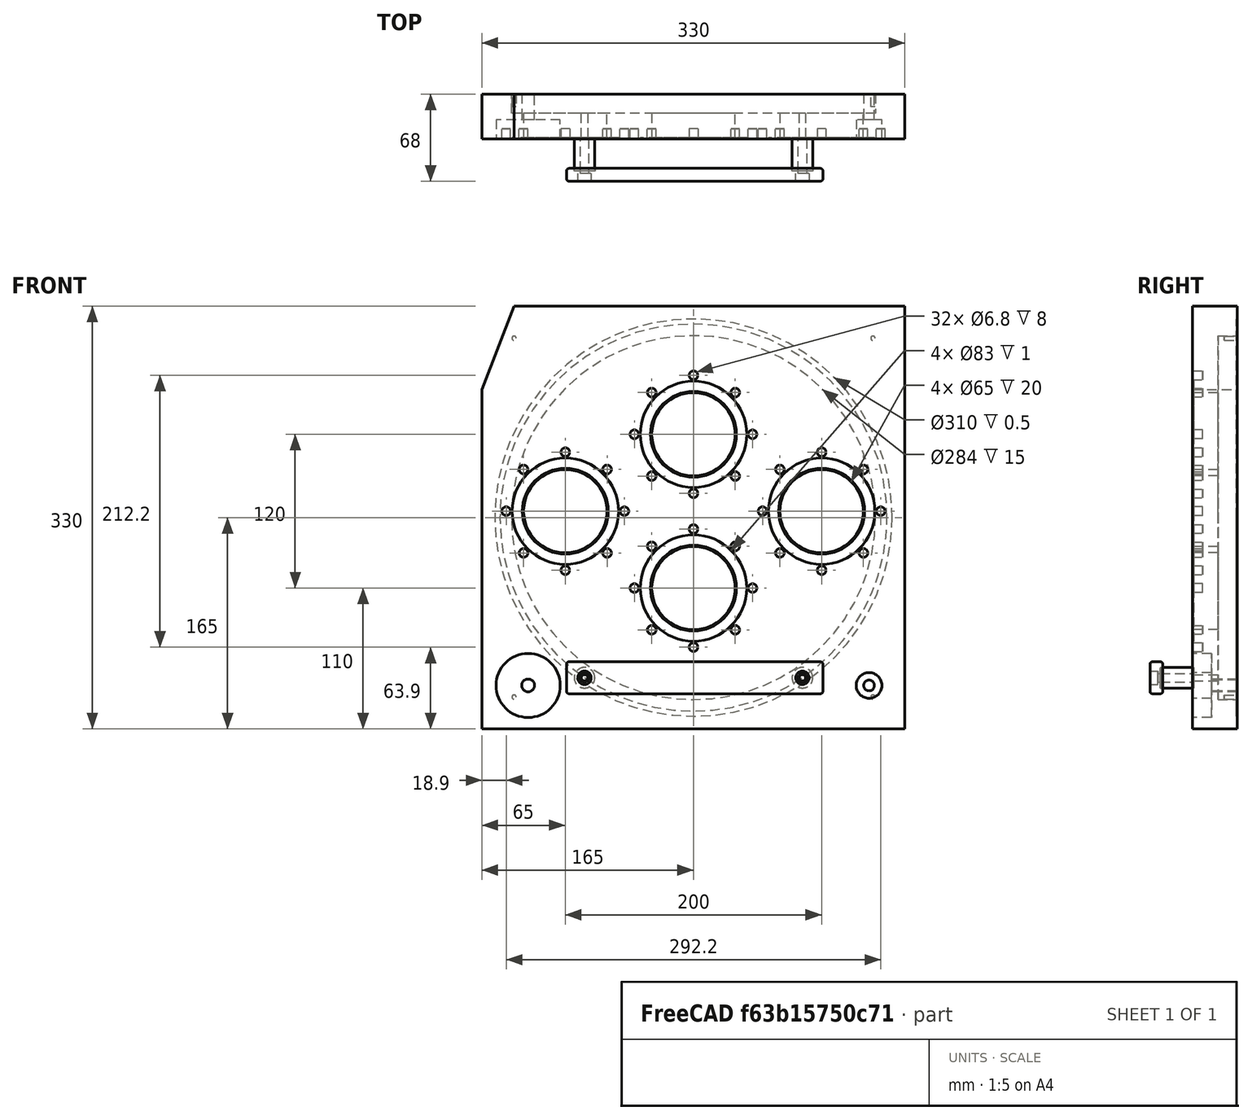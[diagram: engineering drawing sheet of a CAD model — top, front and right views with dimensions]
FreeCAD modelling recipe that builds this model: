
FCSTD DOCUMENT  (FreeCAD 0.21R33675 (Git))
Label: XL30Frontdoor_Flanges01
License: All rights reserved
LicenseURL: http://en.wikipedia.org/wiki/All_rights_reserved
objects: TechDraw::DrawViewDimension×68, Part::Cylinder×54, Part::Compound×28, TechDraw::DrawProjGroupItem×13, Part::Cut×11, Part::MultiFuse×10, TechDraw::DrawSVGTemplate×7, TechDraw::DrawProjGroup×7, TechDraw::DrawPage×7, TechDraw::DrawViewSection×6, Part::Feature×3, TechDraw::DrawViewAnnotation×3, App::Link×1, Part::Box×1, Part::Fillet×1, TechDraw::DrawViewPart×1
note: 214 computed .brp shape members not serialized (recipe doc carries the construction recipe); baked Part::Feature solids carry a one-line shape summary decoded from their .brp
EXTERNAL_REF file=XL30SimpleFrontdoor01.FCStd obj=Cut012_solid

FEATURE [App::Link] Link  label="XL30SimpleFrontdoor01"
  LinkedObject = -> <external XL30SimpleFrontdoor01.FCStd>#Cut012_solid
FEATURE [Part::Cylinder] Cylinder  label="Zylinder"
  Angle = 360
  AttacherType = Attacher::AttachEngine3D
  FirstAngle = 0
  Height = 40
  Placement = pos=(165,0,110) rot=(-1,0,0;1.5708rad)
  Radius = 32.5
  SecondAngle = 0
FEATURE [Part::Cylinder] Cylinder001  label="Zylinder001"
  Angle = 360
  AttacherType = Attacher::AttachEngine3D
  FirstAngle = 0
  Height = 1
  Placement = pos=(165,0,110) rot=(-1,0,0;1.5708rad)
  Radius = 41.5
  SecondAngle = 0
FEATURE [Part::Cylinder] Cylinder002  label="Zylinder002"
  Angle = 360
  AttacherType = Attacher::AttachEngine3D
  FirstAngle = 0
  Height = 1
  Placement = pos=(165,0,110) rot=(-1,0,0;1.5708rad)
  Radius = 33.5
  SecondAngle = 0
FEATURE [Part::Cut] Cut
  Base = -> Cylinder001
  Tool = -> Cylinder002
FEATURE [Part::Cylinder] Cylinder003  label="Zylinder003"
  Angle = 360
  AttacherType = Attacher::AttachEngine3D
  FirstAngle = 0
  Height = 8
  Placement = pos=(0,0,-46.1) rot=(1,0,0;1.5708rad)
  Radius = 3.4
  SecondAngle = 0
FEATURE [Part::Cylinder] Cylinder004  label="Zylinder004"
  Angle = 360
  AttacherType = Attacher::AttachEngine3D
  FirstAngle = 0
  Height = 8
  Placement = pos=(0,0,-46.1) rot=(1,0,0;1.5708rad)
  Radius = 3.4
  SecondAngle = 0
FEATURE [Part::Compound] Compound
  Links = -> [Cylinder004]
  Placement = pos=(0,0,0) rot=(0,1,0;0.785398rad)
FEATURE [Part::Cylinder] Cylinder005  label="Zylinder005"
  Angle = 360
  AttacherType = Attacher::AttachEngine3D
  FirstAngle = 0
  Height = 8
  Placement = pos=(0,0,-46.1) rot=(1,0,0;1.5708rad)
  Radius = 3.4
  SecondAngle = 0
FEATURE [Part::Compound] Compound001
  Links = -> [Cylinder005]
  Placement = pos=(0,0,0) rot=(0,1,0;1.5708rad)
FEATURE [Part::Cylinder] Cylinder006  label="Zylinder006"
  Angle = 360
  AttacherType = Attacher::AttachEngine3D
  FirstAngle = 0
  Height = 8
  Placement = pos=(0,0,-46.1) rot=(1,0,0;1.5708rad)
  Radius = 3.4
  SecondAngle = 0
FEATURE [Part::Compound] Compound002
  Links = -> [Cylinder006]
  Placement = pos=(0,0,0) rot=(0,1,0;2.35619rad)
FEATURE [Part::Cylinder] Cylinder007  label="Zylinder007"
  Angle = 360
  AttacherType = Attacher::AttachEngine3D
  FirstAngle = 0
  Height = 8
  Placement = pos=(0,0,-46.1) rot=(1,0,0;1.5708rad)
  Radius = 3.4
  SecondAngle = 0
FEATURE [Part::Compound] Compound003
  Links = -> [Cylinder007]
  Placement = pos=(0,0,0) rot=(0,1,0;3.14159rad)
FEATURE [Part::Cylinder] Cylinder008  label="Zylinder008"
  Angle = 360
  AttacherType = Attacher::AttachEngine3D
  FirstAngle = 0
  Height = 8
  Placement = pos=(0,0,-46.1) rot=(1,0,0;1.5708rad)
  Radius = 3.4
  SecondAngle = 0
FEATURE [Part::Compound] Compound004
  Links = -> [Cylinder008]
  Placement = pos=(0,0,0) rot=(0,1,0;3.92699rad)
FEATURE [Part::Cylinder] Cylinder009  label="Zylinder009"
  Angle = 360
  AttacherType = Attacher::AttachEngine3D
  FirstAngle = 0
  Height = 8
  Placement = pos=(0,0,-46.1) rot=(1,0,0;1.5708rad)
  Radius = 3.4
  SecondAngle = 0
FEATURE [Part::Compound] Compound005
  Links = -> [Cylinder009]
  Placement = pos=(0,0,0) rot=(0,-1,0;1.5708rad)
FEATURE [Part::Cylinder] Cylinder010  label="Zylinder010"
  Angle = 360
  AttacherType = Attacher::AttachEngine3D
  FirstAngle = 0
  Height = 8
  Placement = pos=(0,0,-46.1) rot=(1,0,0;1.5708rad)
  Radius = 3.4
  SecondAngle = 0
FEATURE [Part::Compound] Compound006
  Links = -> [Cylinder010]
  Placement = pos=(0,0,0) rot=(0,-1,0;0.785398rad)
FEATURE [Part::MultiFuse] Fusion
  Placement = pos=(165,8,110) rot=(0,0,1;0rad)
  Shapes = -> [Compound006,Compound,Compound001,Compound002,Compound003,Compound004,Compound005,Cylinder003]
FEATURE [Part::MultiFuse] Fusion001
  Shapes = -> [Cut,Cylinder,Fusion]
FEATURE [Part::Cut] Cut001
  Base = -> Link
  Tool = -> Fusion001
FEATURE [Part::Cylinder] Cylinder011  label="Zylinder011"
  Angle = 360
  AttacherType = Attacher::AttachEngine3D
  FirstAngle = 0
  Height = 40
  Placement = pos=(165,0,110) rot=(-1,0,0;1.5708rad)
  Radius = 32.5
  SecondAngle = 0
FEATURE [Part::Cylinder] Cylinder012  label="Zylinder012"
  Angle = 360
  AttacherType = Attacher::AttachEngine3D
  FirstAngle = 0
  Height = 1
  Placement = pos=(165,0,110) rot=(-1,0,0;1.5708rad)
  Radius = 41.5
  SecondAngle = 0
FEATURE [Part::Cylinder] Cylinder013  label="Zylinder013"
  Angle = 360
  AttacherType = Attacher::AttachEngine3D
  FirstAngle = 0
  Height = 1
  Placement = pos=(165,0,110) rot=(-1,0,0;1.5708rad)
  Radius = 33.5
  SecondAngle = 0
FEATURE [Part::Cut] Cut002
  Base = -> Cylinder012
  Tool = -> Cylinder013
FEATURE [Part::Cylinder] Cylinder014  label="Zylinder014"
  Angle = 360
  AttacherType = Attacher::AttachEngine3D
  FirstAngle = 0
  Height = 8
  Placement = pos=(0,0,-46.1) rot=(1,0,0;1.5708rad)
  Radius = 3.4
  SecondAngle = 0
FEATURE [Part::Cylinder] Cylinder015  label="Zylinder015"
  Angle = 360
  AttacherType = Attacher::AttachEngine3D
  FirstAngle = 0
  Height = 8
  Placement = pos=(0,0,-46.1) rot=(1,0,0;1.5708rad)
  Radius = 3.4
  SecondAngle = 0
FEATURE [Part::Compound] Compound007
  Links = -> [Cylinder015]
  Placement = pos=(0,0,0) rot=(0,1,0;0.785398rad)
FEATURE [Part::Cylinder] Cylinder016  label="Zylinder016"
  Angle = 360
  AttacherType = Attacher::AttachEngine3D
  FirstAngle = 0
  Height = 8
  Placement = pos=(0,0,-46.1) rot=(1,0,0;1.5708rad)
  Radius = 3.4
  SecondAngle = 0
FEATURE [Part::Compound] Compound008
  Links = -> [Cylinder016]
  Placement = pos=(0,0,0) rot=(0,1,0;1.5708rad)
FEATURE [Part::Cylinder] Cylinder017  label="Zylinder017"
  Angle = 360
  AttacherType = Attacher::AttachEngine3D
  FirstAngle = 0
  Height = 8
  Placement = pos=(0,0,-46.1) rot=(1,0,0;1.5708rad)
  Radius = 3.4
  SecondAngle = 0
FEATURE [Part::Compound] Compound009
  Links = -> [Cylinder017]
  Placement = pos=(0,0,0) rot=(0,1,0;2.35619rad)
FEATURE [Part::Cylinder] Cylinder018  label="Zylinder018"
  Angle = 360
  AttacherType = Attacher::AttachEngine3D
  FirstAngle = 0
  Height = 8
  Placement = pos=(0,0,-46.1) rot=(1,0,0;1.5708rad)
  Radius = 3.4
  SecondAngle = 0
FEATURE [Part::Compound] Compound010
  Links = -> [Cylinder018]
  Placement = pos=(0,0,0) rot=(0,1,0;3.14159rad)
FEATURE [Part::Cylinder] Cylinder019  label="Zylinder019"
  Angle = 360
  AttacherType = Attacher::AttachEngine3D
  FirstAngle = 0
  Height = 8
  Placement = pos=(0,0,-46.1) rot=(1,0,0;1.5708rad)
  Radius = 3.4
  SecondAngle = 0
FEATURE [Part::Compound] Compound011
  Links = -> [Cylinder019]
  Placement = pos=(0,0,0) rot=(0,1,0;3.92699rad)
FEATURE [Part::Cylinder] Cylinder020  label="Zylinder020"
  Angle = 360
  AttacherType = Attacher::AttachEngine3D
  FirstAngle = 0
  Height = 8
  Placement = pos=(0,0,-46.1) rot=(1,0,0;1.5708rad)
  Radius = 3.4
  SecondAngle = 0
FEATURE [Part::Compound] Compound012
  Links = -> [Cylinder020]
  Placement = pos=(0,0,0) rot=(0,-1,0;1.5708rad)
FEATURE [Part::Cylinder] Cylinder021  label="Zylinder021"
  Angle = 360
  AttacherType = Attacher::AttachEngine3D
  FirstAngle = 0
  Height = 8
  Placement = pos=(0,0,-46.1) rot=(1,0,0;1.5708rad)
  Radius = 3.4
  SecondAngle = 0
FEATURE [Part::Compound] Compound013
  Links = -> [Cylinder021]
  Placement = pos=(0,0,0) rot=(0,-1,0;0.785398rad)
FEATURE [Part::MultiFuse] Fusion002
  Placement = pos=(165,8,110) rot=(0,0,1;0rad)
  Shapes = -> [Compound013,Compound007,Compound008,Compound009,Compound010,Compound011,Compound012,Cylinder014]
FEATURE [Part::MultiFuse] Fusion003
  Placement = pos=(0,0,120) rot=(0,0,1;0rad)
  Shapes = -> [Cut002,Cylinder011,Fusion002]
FEATURE [Part::Cylinder] Cylinder022  label="Zylinder022"
  Angle = 360
  AttacherType = Attacher::AttachEngine3D
  FirstAngle = 0
  Height = 40
  Placement = pos=(165,0,110) rot=(-1,0,0;1.5708rad)
  Radius = 32.5
  SecondAngle = 0
FEATURE [Part::Cylinder] Cylinder023  label="Zylinder023"
  Angle = 360
  AttacherType = Attacher::AttachEngine3D
  FirstAngle = 0
  Height = 1
  Placement = pos=(165,0,110) rot=(-1,0,0;1.5708rad)
  Radius = 41.5
  SecondAngle = 0
FEATURE [Part::Cylinder] Cylinder024  label="Zylinder024"
  Angle = 360
  AttacherType = Attacher::AttachEngine3D
  FirstAngle = 0
  Height = 1
  Placement = pos=(165,0,110) rot=(-1,0,0;1.5708rad)
  Radius = 33.5
  SecondAngle = 0
FEATURE [Part::Cut] Cut003
  Base = -> Cylinder023
  Tool = -> Cylinder024
FEATURE [Part::Cylinder] Cylinder025  label="Zylinder025"
  Angle = 360
  AttacherType = Attacher::AttachEngine3D
  FirstAngle = 0
  Height = 8
  Placement = pos=(0,0,-46.1) rot=(1,0,0;1.5708rad)
  Radius = 3.4
  SecondAngle = 0
FEATURE [Part::Cylinder] Cylinder026  label="Zylinder026"
  Angle = 360
  AttacherType = Attacher::AttachEngine3D
  FirstAngle = 0
  Height = 8
  Placement = pos=(0,0,-46.1) rot=(1,0,0;1.5708rad)
  Radius = 3.4
  SecondAngle = 0
FEATURE [Part::Compound] Compound014
  Links = -> [Cylinder026]
  Placement = pos=(0,0,0) rot=(0,1,0;0.785398rad)
FEATURE [Part::Cylinder] Cylinder027  label="Zylinder027"
  Angle = 360
  AttacherType = Attacher::AttachEngine3D
  FirstAngle = 0
  Height = 8
  Placement = pos=(0,0,-46.1) rot=(1,0,0;1.5708rad)
  Radius = 3.4
  SecondAngle = 0
FEATURE [Part::Compound] Compound015
  Links = -> [Cylinder027]
  Placement = pos=(0,0,0) rot=(0,1,0;1.5708rad)
FEATURE [Part::Cylinder] Cylinder028  label="Zylinder028"
  Angle = 360
  AttacherType = Attacher::AttachEngine3D
  FirstAngle = 0
  Height = 8
  Placement = pos=(0,0,-46.1) rot=(1,0,0;1.5708rad)
  Radius = 3.4
  SecondAngle = 0
FEATURE [Part::Compound] Compound016
  Links = -> [Cylinder028]
  Placement = pos=(0,0,0) rot=(0,1,0;2.35619rad)
FEATURE [Part::Cylinder] Cylinder029  label="Zylinder029"
  Angle = 360
  AttacherType = Attacher::AttachEngine3D
  FirstAngle = 0
  Height = 8
  Placement = pos=(0,0,-46.1) rot=(1,0,0;1.5708rad)
  Radius = 3.4
  SecondAngle = 0
FEATURE [Part::Compound] Compound017
  Links = -> [Cylinder029]
  Placement = pos=(0,0,0) rot=(0,1,0;3.14159rad)
FEATURE [Part::Cylinder] Cylinder030  label="Zylinder030"
  Angle = 360
  AttacherType = Attacher::AttachEngine3D
  FirstAngle = 0
  Height = 8
  Placement = pos=(0,0,-46.1) rot=(1,0,0;1.5708rad)
  Radius = 3.4
  SecondAngle = 0
FEATURE [Part::Compound] Compound018
  Links = -> [Cylinder030]
  Placement = pos=(0,0,0) rot=(0,1,0;3.92699rad)
FEATURE [Part::Cylinder] Cylinder031  label="Zylinder031"
  Angle = 360
  AttacherType = Attacher::AttachEngine3D
  FirstAngle = 0
  Height = 8
  Placement = pos=(0,0,-46.1) rot=(1,0,0;1.5708rad)
  Radius = 3.4
  SecondAngle = 0
FEATURE [Part::Compound] Compound019
  Links = -> [Cylinder031]
  Placement = pos=(0,0,0) rot=(0,-1,0;1.5708rad)
FEATURE [Part::Cylinder] Cylinder032  label="Zylinder032"
  Angle = 360
  AttacherType = Attacher::AttachEngine3D
  FirstAngle = 0
  Height = 8
  Placement = pos=(0,0,-46.1) rot=(1,0,0;1.5708rad)
  Radius = 3.4
  SecondAngle = 0
FEATURE [Part::Compound] Compound020
  Links = -> [Cylinder032]
  Placement = pos=(0,0,0) rot=(0,-1,0;0.785398rad)
FEATURE [Part::MultiFuse] Fusion004
  Placement = pos=(165,8,110) rot=(0,0,1;0rad)
  Shapes = -> [Compound020,Compound014,Compound015,Compound016,Compound017,Compound018,Compound019,Cylinder025]
FEATURE [Part::MultiFuse] Fusion005
  Placement = pos=(-100,0,60) rot=(0,0,1;0rad)
  Shapes = -> [Cut003,Cylinder022,Fusion004]
FEATURE [Part::Cylinder] Cylinder033  label="Zylinder033"
  Angle = 360
  AttacherType = Attacher::AttachEngine3D
  FirstAngle = 0
  Height = 40
  Placement = pos=(165,0,110) rot=(-1,0,0;1.5708rad)
  Radius = 32.5
  SecondAngle = 0
FEATURE [Part::Cylinder] Cylinder034  label="Zylinder034"
  Angle = 360
  AttacherType = Attacher::AttachEngine3D
  FirstAngle = 0
  Height = 1
  Placement = pos=(165,0,110) rot=(-1,0,0;1.5708rad)
  Radius = 41.5
  SecondAngle = 0
FEATURE [Part::Cylinder] Cylinder035  label="Zylinder035"
  Angle = 360
  AttacherType = Attacher::AttachEngine3D
  FirstAngle = 0
  Height = 1
  Placement = pos=(165,0,110) rot=(-1,0,0;1.5708rad)
  Radius = 33.5
  SecondAngle = 0
FEATURE [Part::Cut] Cut004
  Base = -> Cylinder034
  Tool = -> Cylinder035
FEATURE [Part::Cylinder] Cylinder036  label="Zylinder036"
  Angle = 360
  AttacherType = Attacher::AttachEngine3D
  FirstAngle = 0
  Height = 8
  Placement = pos=(0,0,-46.1) rot=(1,0,0;1.5708rad)
  Radius = 3.4
  SecondAngle = 0
FEATURE [Part::Cylinder] Cylinder037  label="Zylinder037"
  Angle = 360
  AttacherType = Attacher::AttachEngine3D
  FirstAngle = 0
  Height = 8
  Placement = pos=(0,0,-46.1) rot=(1,0,0;1.5708rad)
  Radius = 3.4
  SecondAngle = 0
FEATURE [Part::Compound] Compound021
  Links = -> [Cylinder037]
  Placement = pos=(0,0,0) rot=(0,1,0;0.785398rad)
FEATURE [Part::Cylinder] Cylinder038  label="Zylinder038"
  Angle = 360
  AttacherType = Attacher::AttachEngine3D
  FirstAngle = 0
  Height = 8
  Placement = pos=(0,0,-46.1) rot=(1,0,0;1.5708rad)
  Radius = 3.4
  SecondAngle = 0
FEATURE [Part::Compound] Compound022
  Links = -> [Cylinder038]
  Placement = pos=(0,0,0) rot=(0,1,0;1.5708rad)
FEATURE [Part::Cylinder] Cylinder039  label="Zylinder039"
  Angle = 360
  AttacherType = Attacher::AttachEngine3D
  FirstAngle = 0
  Height = 8
  Placement = pos=(0,0,-46.1) rot=(1,0,0;1.5708rad)
  Radius = 3.4
  SecondAngle = 0
FEATURE [Part::Compound] Compound023
  Links = -> [Cylinder039]
  Placement = pos=(0,0,0) rot=(0,1,0;2.35619rad)
FEATURE [Part::Cylinder] Cylinder040  label="Zylinder040"
  Angle = 360
  AttacherType = Attacher::AttachEngine3D
  FirstAngle = 0
  Height = 8
  Placement = pos=(0,0,-46.1) rot=(1,0,0;1.5708rad)
  Radius = 3.4
  SecondAngle = 0
FEATURE [Part::Compound] Compound024
  Links = -> [Cylinder040]
  Placement = pos=(0,0,0) rot=(0,1,0;3.14159rad)
FEATURE [Part::Cylinder] Cylinder041  label="Zylinder041"
  Angle = 360
  AttacherType = Attacher::AttachEngine3D
  FirstAngle = 0
  Height = 8
  Placement = pos=(0,0,-46.1) rot=(1,0,0;1.5708rad)
  Radius = 3.4
  SecondAngle = 0
FEATURE [Part::Compound] Compound025
  Links = -> [Cylinder041]
  Placement = pos=(0,0,0) rot=(0,1,0;3.92699rad)
FEATURE [Part::Cylinder] Cylinder042  label="Zylinder042"
  Angle = 360
  AttacherType = Attacher::AttachEngine3D
  FirstAngle = 0
  Height = 8
  Placement = pos=(0,0,-46.1) rot=(1,0,0;1.5708rad)
  Radius = 3.4
  SecondAngle = 0
FEATURE [Part::Compound] Compound026
  Links = -> [Cylinder042]
  Placement = pos=(0,0,0) rot=(0,-1,0;1.5708rad)
FEATURE [Part::Cylinder] Cylinder043  label="Zylinder043"
  Angle = 360
  AttacherType = Attacher::AttachEngine3D
  FirstAngle = 0
  Height = 8
  Placement = pos=(0,0,-46.1) rot=(1,0,0;1.5708rad)
  Radius = 3.4
  SecondAngle = 0
FEATURE [Part::Compound] Compound027
  Links = -> [Cylinder043]
  Placement = pos=(0,0,0) rot=(0,-1,0;0.785398rad)
FEATURE [Part::MultiFuse] Fusion006
  Placement = pos=(165,8,110) rot=(0,0,1;0rad)
  Shapes = -> [Compound027,Compound021,Compound022,Compound023,Compound024,Compound025,Compound026,Cylinder036]
FEATURE [Part::MultiFuse] Fusion007
  Placement = pos=(100,0,60) rot=(0,0,1;0rad)
  Shapes = -> [Cut004,Cylinder033,Fusion006]
FEATURE [Part::MultiFuse] Fusion008
  Shapes = -> [Fusion003,Fusion007,Fusion005]
FEATURE [Part::Cut] Cut005  label="XL30FrontdoorCF64Flanges"
  Base = -> Cut001
  Tool = -> Fusion008
FEATURE [Part::Feature] Cut005_solid  label="XL30FrontdoorCF64Flanges (Solid)"
  shape: bbox 330 x 35 x 330 mm, 119 faces (baked)
FEATURE [Part::Box] Box002  label="Würfel002"
  AttacherType = Attacher::AttachEngine3D
  Height = 25
  Length = 200
  Placement = pos=(66,-28,27.5) rot=(0,0,1;0rad)
  Width = 10
FEATURE [Part::Cylinder] Cylinder044  label="Zylinder044"
  Angle = 360
  AttacherType = Attacher::AttachEngine3D
  FirstAngle = 0
  Height = 25
  Placement = pos=(80,0,40) rot=(1,0,0;1.5708rad)
  Radius = 8
  SecondAngle = 0
FEATURE [Part::Cylinder] Cylinder045  label="Zylinder045"
  Angle = 360
  AttacherType = Attacher::AttachEngine3D
  FirstAngle = 0
  Height = 25
  Placement = pos=(250,0,40) rot=(1,0,0;1.5708rad)
  Radius = 8
  SecondAngle = 0
FEATURE [Part::Cylinder] Cylinder046  label="Zylinder046"
  Angle = 360
  AttacherType = Attacher::AttachEngine3D
  FirstAngle = 0
  Height = 25
  Placement = pos=(80,0,40) rot=(1,0,0;1.5708rad)
  Radius = 3.3
  SecondAngle = 0
FEATURE [Part::Cut] Cut006  label="Spacer01"
  Base = -> Cylinder044
  Tool = -> Cylinder046
FEATURE [Part::Cylinder] Cylinder047  label="Zylinder047"
  Angle = 360
  AttacherType = Attacher::AttachEngine3D
  FirstAngle = 0
  Height = 25
  Placement = pos=(250,0,40) rot=(1,0,0;1.5708rad)
  Radius = 3.3
  SecondAngle = 0
FEATURE [Part::Cut] Cut007  label="Spacer02"
  Base = -> Cylinder045
  Tool = -> Cylinder047
FEATURE [Part::Cylinder] Cylinder048  label="Zylinder048"
  Angle = 360
  AttacherType = Attacher::AttachEngine3D
  FirstAngle = 0
  Height = 20
  Placement = pos=(80,0,40) rot=(1,0,0;1.5708rad)
  Radius = 8.1
  SecondAngle = 0
FEATURE [Part::Cut] Cut008
  Base = -> Box002
  Tool = -> Cylinder048
FEATURE [Part::Cylinder] Cylinder049  label="Zylinder049"
  Angle = 360
  AttacherType = Attacher::AttachEngine3D
  FirstAngle = 0
  Height = 20
  Placement = pos=(250,0,40) rot=(1,0,0;1.5708rad)
  Radius = 8.1
  SecondAngle = 0
FEATURE [Part::Cut] Cut009
  Base = -> Cut008
  Tool = -> Cylinder049
FEATURE [Part::Cylinder] Cylinder050  label="Zylinder050"
  Angle = 360
  AttacherType = Attacher::AttachEngine3D
  FirstAngle = 0
  Height = 6
  Placement = pos=(80,-22,40) rot=(1,0,0;1.5708rad)
  Radius = 5.2
  SecondAngle = 0
FEATURE [Part::Cylinder] Cylinder051  label="Zylinder051"
  Angle = 360
  AttacherType = Attacher::AttachEngine3D
  FirstAngle = 0
  Height = 6
  Placement = pos=(250,-22,40) rot=(1,0,0;1.5708rad)
  Radius = 5.2
  SecondAngle = 0
FEATURE [Part::Cylinder] Cylinder052  label="Zylinder052"
  Angle = 360
  AttacherType = Attacher::AttachEngine3D
  FirstAngle = 0
  Height = 20
  Placement = pos=(80,-10,40) rot=(1,0,0;1.5708rad)
  Radius = 3.3
  SecondAngle = 0
FEATURE [Part::Cylinder] Cylinder053  label="Zylinder053"
  Angle = 360
  AttacherType = Attacher::AttachEngine3D
  FirstAngle = 0
  Height = 20
  Placement = pos=(250,-10,40) rot=(1,0,0;1.5708rad)
  Radius = 3.3
  SecondAngle = 0
FEATURE [Part::MultiFuse] Fusion009
  Shapes = -> [Cylinder050,Cylinder051,Cylinder052,Cylinder053]
FEATURE [Part::Cut] Cut010  label="HandleWithoutPhases"
  Base = -> Cut009
  Tool = -> Fusion009
FEATURE [Part::Fillet] Fillet  label="HandleWithFillet"
  Base = -> Cut010
  Edges = 12 edges r=2: [Edge1,Edge2,Edge3,Edge4,Edge5,Edge6,Edge7,Edge10,Edge11,Edge12,Edge13,Edge16]
  Placement = pos=(0,-5,0) rot=(0,0,1;0rad)
FEATURE [Part::Feature] Cut006_solid  label="XL30FrontdoorCF64Flanges_Spacer"
  shape: bbox 16 x 25 x 16 mm, 4 faces (baked)
FEATURE [Part::Feature] Fillet_solid  label="XL30FrontdoorCF64Flanges_Handle"
  shape: bbox 200 x 10 x 25 mm, 36 faces (baked)
FEATURE [TechDraw::DrawSVGTemplate] Template
  EditableTexts = Designed_by_Name=Thomas Spielauer; Drawing_number=1; FC-Date=2023-09-05; FC-SC=mm; FC-SH=1/1; FC-Title=XL30 compatible flange door; Subtitle=Handle
  Height = 210
  Orientation = 1
  Template = <path>
  Width = 297
FEATURE [TechDraw::DrawProjGroupItem] ProjItem  label="Front"
  CoarseView = false
  Direction = (0,-1,0)
  Focus = 100
  HardHidden = false
  IsoCount = 0
  IsoHidden = false
  IsoVisible = false
  LockPosition = true
  Perspective = false
  Rotation = 0
  RotationVector = (1,0,0)
  ScaleType = 2
  ScrubCount = 0
  SeamHidden = false
  SeamVisible = false
  SmoothHidden = false
  SmoothVisible = true
  Source = -> [Fillet_solid]
  Type = 0
  X = 0
  XDirection = (1,0,0)
  Y = 0
FEATURE [TechDraw::DrawProjGroupItem] ProjItem001  label="Left"
  CoarseView = false
  Direction = (-1,-1e-16,0)
  Focus = 100
  HardHidden = false
  IsoCount = 0
  IsoHidden = false
  IsoVisible = false
  LockPosition = false
  Perspective = false
  Rotation = 0
  RotationVector = (1,0,0)
  ScaleType = 2
  ScrubCount = 0
  SeamHidden = false
  SeamVisible = false
  SmoothHidden = false
  SmoothVisible = true
  Source = -> [Fillet_solid]
  Type = 1
  X = 134.42
  XDirection = (1e-16,-1,0)
  Y = 0
FEATURE [TechDraw::DrawProjGroupItem] ProjItem002  label="Bottom"
  CoarseView = false
  Direction = (0,0,-1)
  Focus = 100
  HardHidden = false
  IsoCount = 0
  IsoHidden = false
  IsoVisible = false
  LockPosition = false
  Perspective = false
  Rotation = 0
  RotationVector = (1,0,0)
  ScaleType = 2
  ScrubCount = 0
  SeamHidden = false
  SeamVisible = false
  SmoothHidden = false
  SmoothVisible = true
  Source = -> [Fillet_solid]
  Type = 5
  X = 0
  XDirection = (1,0,0)
  Y = 41.7139
FEATURE [TechDraw::DrawProjGroup] ProjGroup
  Anchor = -> ProjItem
  AutoDistribute = false
  LockPosition = false
  ProjectionType = 0
  Rotation = 0
  ScaleType = 0
  Source = -> [Fillet_solid]
  Views = -> [ProjItem,ProjItem001,ProjItem002]
  X = 120.858
  Y = 131.49
  spacingX = 15
  spacingY = 15
FEATURE [TechDraw::DrawProjGroupItem] ProjItem003  label="Rückseite"
  CoarseView = false
  Direction = (0,1,0)
  Focus = 100
  HardHidden = false
  IsoCount = 0
  IsoHidden = false
  IsoVisible = false
  LockPosition = true
  Perspective = false
  Rotation = 0
  RotationVector = (-1,0,0)
  ScaleType = 2
  ScrubCount = 0
  SeamHidden = false
  SeamVisible = false
  SmoothHidden = false
  SmoothVisible = true
  Source = -> [Fillet_solid]
  Type = 0
  X = 0
  XDirection = (-1,0,0)
  Y = 0
FEATURE [TechDraw::DrawProjGroup] ProjGroup001
  Anchor = -> ProjItem003
  AutoDistribute = true
  LockPosition = false
  ProjectionType = 0
  Rotation = 0
  ScaleType = 0
  Source = -> [Fillet_solid]
  Views = -> [ProjItem003]
  X = 123.356
  Y = 85.8274
  spacingX = 15
  spacingY = 15
FEATURE [TechDraw::DrawViewDimension] Dimension
  AngleOverride = false
  Arbitrary = false
  ArbitraryTolerances = false
  EqualTolerance = true
  ExtensionAngle = 0
  FormatSpec = %.2w
  FormatSpecOverTolerance = %+.2w
  FormatSpecUnderTolerance = %+.2w
  Inverted = false
  LineAngle = 0
  LockPosition = false
  MeasureType = 1
  OverTolerance = 0
  References2D = -> [ProjItem]
  Rotation = 0
  ScaleType = 0
  TheoreticalExact = false
  Type = 0
  UnderTolerance = 0
  X = 116.037
  Y = 2.5
FEATURE [TechDraw::DrawViewDimension] Dimension002
  AngleOverride = false
  Arbitrary = false
  ArbitraryTolerances = false
  EqualTolerance = true
  ExtensionAngle = 0
  FormatSpec = %.2w
  FormatSpecOverTolerance = %+.2w
  FormatSpecUnderTolerance = %+.2w
  Inverted = false
  LineAngle = 0
  LockPosition = false
  MeasureType = 1
  OverTolerance = 0
  References2D = -> [ProjItem002]
  Rotation = 0
  ScaleType = 0
  TheoreticalExact = false
  Type = 0
  UnderTolerance = 0
  X = 116.016
  Y = 2.95828
FEATURE [TechDraw::DrawViewDimension] Dimension003
  AngleOverride = false
  Arbitrary = false
  ArbitraryTolerances = false
  EqualTolerance = true
  ExtensionAngle = 0
  FormatSpec = %.2w
  FormatSpecOverTolerance = %+.2w
  FormatSpecUnderTolerance = %+.2w
  Inverted = false
  LineAngle = 0
  LockPosition = false
  MeasureType = 1
  OverTolerance = 0
  References2D = -> [ProjItem001]
  Rotation = 0
  ScaleType = 0
  TheoreticalExact = false
  Type = 0
  UnderTolerance = 0
  X = -0.639485
  Y = 23.4627
FEATURE [TechDraw::DrawViewDimension] Dimension004
  AngleOverride = false
  Arbitrary = false
  ArbitraryTolerances = false
  EqualTolerance = true
  ExtensionAngle = 0
  FormatSpec = ⌀%.2w
  FormatSpecOverTolerance = %+.2w
  FormatSpecUnderTolerance = %+.2w
  Inverted = false
  LineAngle = 0
  LockPosition = false
  MeasureType = 1
  OverTolerance = 0
  References2D = -> [ProjItem]
  Rotation = 0
  ScaleType = 0
  TheoreticalExact = false
  Type = 5
  UnderTolerance = 0
  X = -73.0563
  Y = 21.9408
FEATURE [TechDraw::DrawViewDimension] Dimension005
  AngleOverride = false
  Arbitrary = false
  ArbitraryTolerances = false
  EqualTolerance = true
  ExtensionAngle = 0
  FormatSpec = ⌀%.2w
  FormatSpecOverTolerance = %+.2w
  FormatSpecUnderTolerance = %+.2w
  Inverted = false
  LineAngle = 0
  LockPosition = false
  MeasureType = 1
  OverTolerance = 0
  References2D = -> [ProjItem]
  Rotation = 0
  ScaleType = 0
  TheoreticalExact = false
  Type = 5
  UnderTolerance = 0
  X = -60.6549
  Y = -17.1005
FEATURE [TechDraw::DrawViewDimension] Dimension006
  AngleOverride = false
  Arbitrary = false
  ArbitraryTolerances = false
  EqualTolerance = true
  ExtensionAngle = 0
  FormatSpec = ⌀%.2w
  FormatSpecOverTolerance = %+.2w
  FormatSpecUnderTolerance = %+.2w
  Inverted = false
  LineAngle = 0
  LockPosition = false
  MeasureType = 1
  OverTolerance = 0
  References2D = -> [ProjItem003]
  Rotation = 0
  ScaleType = 0
  TheoreticalExact = false
  Type = 5
  UnderTolerance = 0
  X = -59.3899
  Y = 7.15876
FEATURE [TechDraw::DrawViewDimension] Dimension007
  AngleOverride = false
  Arbitrary = false
  ArbitraryTolerances = false
  EqualTolerance = true
  ExtensionAngle = 0
  FormatSpec = %.2w
  FormatSpecOverTolerance = %+.2w
  FormatSpecUnderTolerance = %+.2w
  Inverted = false
  LineAngle = 0
  LockPosition = false
  MeasureType = 1
  OverTolerance = 0
  References2D = -> [ProjItem]
  Rotation = 0
  ScaleType = 0
  TheoreticalExact = false
  Type = 0
  UnderTolerance = 0
  X = -92.8209
  Y = 23.2929
FEATURE [TechDraw::DrawViewDimension] Dimension008
  AngleOverride = false
  Arbitrary = false
  ArbitraryTolerances = false
  EqualTolerance = true
  ExtensionAngle = 0
  FormatSpec = %.2w
  FormatSpecOverTolerance = %+.2w
  FormatSpecUnderTolerance = %+.2w
  Inverted = false
  LineAngle = 0
  LockPosition = false
  MeasureType = 1
  OverTolerance = 0
  References2D = -> [ProjItem]
  Rotation = 0
  ScaleType = 0
  TheoreticalExact = false
  Type = 0
  UnderTolerance = 0
  X = -104.358
  Y = -2.28444
FEATURE [TechDraw::DrawViewDimension] Dimension009
  AngleOverride = false
  Arbitrary = false
  ArbitraryTolerances = false
  EqualTolerance = true
  ExtensionAngle = 0
  FormatSpec = %.2w
  FormatSpecOverTolerance = %+.2w
  FormatSpecUnderTolerance = %+.2w
  Inverted = false
  LineAngle = 0
  LockPosition = false
  MeasureType = 1
  OverTolerance = 0
  References2D = -> [ProjItem002]
  Rotation = 0
  ScaleType = 0
  TheoreticalExact = false
  Type = 0
  UnderTolerance = 0
  X = -0.551133
  Y = 19.0028
FEATURE [TechDraw::DrawViewSection] SectionView  label="Section  - "
  BaseView = -> ProjItem003
  CoarseView = false
  CutSurfaceDisplay = 2
  Direction = (1,0,-1e-16)
  FileGeomPattern = <path>
  FileHatchPattern = <path>
  Focus = 100
  FuseBeforeCut = false
  HardHidden = false
  HatchOffset = (0,0,0)
  HatchRotation = 0
  HatchScale = 1
  IsoCount = 0
  IsoHidden = false
  IsoVisible = false
  LockPosition = false
  NameGeomPattern = Diamant
  Perspective = false
  Rotation = -90
  ScaleType = 2
  ScrubCount = 0
  SeamHidden = false
  SeamVisible = false
  SectionDirection = 4
  SectionNormal = (1,0,-1e-16)
  SectionOrigin = (80,-28,40)
  SmoothHidden = false
  SmoothVisible = true
  Source = -> [Fillet_solid]
  TrimAfterCut = false
  X = 255.524
  XDirection = (-1e-16,0,-1)
  Y = 85.6829
FEATURE [TechDraw::DrawViewDimension] Dimension010
  AngleOverride = false
  Arbitrary = false
  ArbitraryTolerances = false
  EqualTolerance = true
  ExtensionAngle = 0
  FormatSpec = %.2w
  FormatSpecOverTolerance = %+.2w
  FormatSpecUnderTolerance = %+.2w
  Inverted = false
  LineAngle = 0
  LockPosition = false
  MeasureType = 1
  OverTolerance = 0
  References2D = -> [SectionView]
  Rotation = 0
  ScaleType = 0
  TheoreticalExact = false
  Type = 0
  UnderTolerance = 0
  X = -10.101
  Y = 21.7017
FEATURE [TechDraw::DrawViewDimension] Dimension011
  AngleOverride = false
  Arbitrary = false
  ArbitraryTolerances = false
  EqualTolerance = true
  ExtensionAngle = 0
  FormatSpec = %.2w
  FormatSpecOverTolerance = %+.2w
  FormatSpecUnderTolerance = %+.2w
  Inverted = false
  LineAngle = 0
  LockPosition = false
  MeasureType = 1
  OverTolerance = 0
  References2D = -> [SectionView]
  Rotation = 0
  ScaleType = 0
  TheoreticalExact = false
  Type = 0
  UnderTolerance = 0
  X = 10.3313
  Y = -12.0118
FEATURE [TechDraw::DrawViewDimension] Dimension012
  AngleOverride = false
  Arbitrary = false
  ArbitraryTolerances = false
  EqualTolerance = true
  ExtensionAngle = 0
  FormatSpec = %.2w
  FormatSpecOverTolerance = %+.2w
  FormatSpecUnderTolerance = %+.2w
  Inverted = false
  LineAngle = 0
  LockPosition = false
  MeasureType = 1
  OverTolerance = 0
  References2D = -> [SectionView]
  Rotation = 0
  ScaleType = 0
  TheoreticalExact = false
  Type = 0
  UnderTolerance = 0
  X = -20.7894
  Y = -9.42975
FEATURE [TechDraw::DrawViewDimension] Dimension013
  AngleOverride = false
  Arbitrary = false
  ArbitraryTolerances = false
  EqualTolerance = true
  ExtensionAngle = 0
  FormatSpec = %.2w
  FormatSpecOverTolerance = %+.2w
  FormatSpecUnderTolerance = %+.2w
  Inverted = false
  LineAngle = 0
  LockPosition = false
  MeasureType = 1
  OverTolerance = 0
  References2D = -> [SectionView]
  Rotation = 0
  ScaleType = 0
  TheoreticalExact = false
  Type = 0
  UnderTolerance = 0
  X = -17.7718
  Y = 16.1841
FEATURE [TechDraw::DrawViewDimension] Dimension014
  AngleOverride = false
  Arbitrary = false
  ArbitraryTolerances = false
  EqualTolerance = true
  ExtensionAngle = 0
  FormatSpec = %.2w
  FormatSpecOverTolerance = %+.2w
  FormatSpecUnderTolerance = %+.2w
  Inverted = false
  LineAngle = 0
  LockPosition = false
  MeasureType = 1
  OverTolerance = 0
  References2D = -> [SectionView]
  Rotation = 0
  ScaleType = 0
  TheoreticalExact = false
  Type = 0
  UnderTolerance = 0
  X = 16.5087
  Y = 16.7104
FEATURE [TechDraw::DrawViewAnnotation] Annotation
  Font = osifont
  LineSpace = 100
  LockPosition = false
  MaxWidth = -1
  Rotation = 0
  ScaleType = 0
  Text = Material can be aluminum or steel, | the form of the chamfer is uncritical | and only for comfortable usage
  TextSize = 5
  TextStyle = 0
  X = 76.4665
  Y = 31.6954
FEATURE [TechDraw::DrawPage] Page  label="HandleDrawing"
  KeepUpdated = true
  NextBalloonIndex = 1
  ProjectionType = 0
  Template = -> Template
  Views = -> [ProjGroup,ProjGroup001,Dimension,Dimension002,Dimension003,Dimension004,Dimension005,Dimension006,Dimension007,Dimension008,Dimension009,SectionView,Dimension010,Dimension011,Dimension012,Dimension013,Dimension014,Annotation]
FEATURE [TechDraw::DrawSVGTemplate] Template001
  EditableTexts = Designed_by_Name=Thomas Spielauer; Drawing_number=1/1; FC-Date=2023-09-05; FC-SC=mm; FC-SH=1/1; FC-Title=XL30 compatible flange door; Subtitle=Handle spacer
  Height = 210
  Orientation = 1
  Template = <path>
  Width = 297
FEATURE [TechDraw::DrawProjGroupItem] ProjItem004  label="Front001"
  CoarseView = false
  Direction = (0,1,0)
  Focus = 100
  HardHidden = false
  IsoCount = 0
  IsoHidden = false
  IsoVisible = false
  LockPosition = true
  Perspective = false
  Rotation = 0
  RotationVector = (-1,0,0)
  Scale = 2
  ScaleType = 2
  ScrubCount = 0
  SeamHidden = false
  SeamVisible = false
  SmoothHidden = false
  SmoothVisible = true
  Source = -> [Cut007]
  Type = 0
  X = 0
  XDirection = (-1,0,0)
  Y = 0
FEATURE [TechDraw::DrawProjGroupItem] ProjItem006  label="Bottom001"
  CoarseView = false
  Direction = (0,0,-1)
  Focus = 100
  HardHidden = false
  IsoCount = 0
  IsoHidden = false
  IsoVisible = false
  LockPosition = false
  Perspective = false
  Rotation = 0
  RotationVector = (1,0,0)
  Scale = 2
  ScaleType = 2
  ScrubCount = 0
  SeamHidden = false
  SeamVisible = false
  SmoothHidden = false
  SmoothVisible = true
  Source = -> [Cut007]
  Type = 5
  X = 0
  XDirection = (-1,0,0)
  Y = 56
FEATURE [TechDraw::DrawProjGroup] ProjGroup002
  Anchor = -> ProjItem004
  AutoDistribute = true
  LockPosition = false
  ProjectionType = 0
  Rotation = 0
  Scale = 2
  ScaleType = 2
  Source = -> [Cut007]
  Views = -> [ProjItem004,ProjItem006]
  X = 55.5178
  Y = 91.8181
  spacingX = 15
  spacingY = 15
FEATURE [TechDraw::DrawViewSection] SectionView001  label="Section  - 001"
  BaseView = -> ProjItem006
  CoarseView = false
  CutSurfaceDisplay = 2
  Direction = (1,-1e-16,0)
  FileGeomPattern = <path>
  FileHatchPattern = <path>
  Focus = 100
  FuseBeforeCut = false
  HardHidden = false
  HatchOffset = (0,0,0)
  HatchRotation = 0
  HatchScale = 1
  IsoCount = 0
  IsoHidden = false
  IsoVisible = false
  LockPosition = false
  NameGeomPattern = Diamant
  Perspective = false
  Rotation = -90
  Scale = 2
  ScaleType = 2
  ScrubCount = 0
  SeamHidden = false
  SeamVisible = false
  SectionDirection = 4
  SectionNormal = (1,-1e-16,0)
  SectionOrigin = (250,-13.5,40)
  SmoothHidden = false
  SmoothVisible = true
  Source = -> [Cut007]
  TrimAfterCut = false
  X = 129.274
  XDirection = (-1e-16,-1,0)
  Y = 151.601
FEATURE [TechDraw::DrawViewDimension] Dimension015
  AngleOverride = false
  Arbitrary = false
  ArbitraryTolerances = false
  EqualTolerance = true
  ExtensionAngle = 0
  FormatSpec = %.2w
  FormatSpecOverTolerance = %+.2w
  FormatSpecUnderTolerance = %+.2w
  Inverted = false
  LineAngle = 0
  LockPosition = false
  MeasureType = 1
  OverTolerance = 0
  References2D = -> [ProjItem006]
  Rotation = 0
  ScaleType = 0
  TheoreticalExact = false
  Type = 0
  UnderTolerance = 0
  X = -30.1421
  Y = 2.19032
FEATURE [TechDraw::DrawViewDimension] Dimension016
  AngleOverride = false
  Arbitrary = false
  ArbitraryTolerances = false
  EqualTolerance = true
  ExtensionAngle = 0
  FormatSpec = ⌀%.2w
  FormatSpecOverTolerance = %+.2w
  FormatSpecUnderTolerance = %+.2w
  Inverted = false
  LineAngle = 0
  LockPosition = false
  MeasureType = 1
  OverTolerance = 0
  References2D = -> [ProjItem004]
  Rotation = 0
  ScaleType = 0
  TheoreticalExact = false
  Type = 5
  UnderTolerance = 0
  X = 41.1197
  Y = 13.9766
FEATURE [TechDraw::DrawViewDimension] Dimension017
  AngleOverride = false
  Arbitrary = false
  ArbitraryTolerances = false
  EqualTolerance = true
  ExtensionAngle = 0
  FormatSpec = ⌀%.2w
  FormatSpecOverTolerance = %+.2w
  FormatSpecUnderTolerance = %+.2w
  Inverted = false
  LineAngle = 0
  LockPosition = false
  MeasureType = 1
  OverTolerance = 0
  References2D = -> [ProjItem004]
  Rotation = 0
  ScaleType = 0
  TheoreticalExact = false
  Type = 5
  UnderTolerance = 0
  X = 42.335
  Y = 3.0384
FEATURE [TechDraw::DrawViewAnnotation] Annotation001
  Font = osifont
  LineSpace = 100
  LockPosition = false
  MaxWidth = -1
  Rotation = 0
  ScaleType = 0
  Text = Two per door
  TextSize = 5
  TextStyle = 0
  X = 263.492
  Y = 67.1873
FEATURE [TechDraw::DrawPage] Page001  label="HandleSpacer"
  KeepUpdated = true
  NextBalloonIndex = 1
  ProjectionType = 0
  Template = -> Template001
  Views = -> [ProjGroup002,SectionView001,Dimension015,Dimension016,Dimension017,Annotation001]
FEATURE [TechDraw::DrawSVGTemplate] Template002
  EditableTexts = Designed_by_Name=Thomas Spielauer; Drawing_number=1; FC-Date=2023-09-05; FC-SC=mm; FC-SH=1/5; FC-Title=XL30 compatible flange door; Subtitle=Main door
  Height = 210
  Orientation = 1
  Template = <path>
  Width = 297
FEATURE [TechDraw::DrawProjGroupItem] ProjItem007  label="Front002"
  CoarseView = false
  Direction = (0,-1,0)
  Focus = 100
  HardHidden = false
  IsoCount = 0
  IsoHidden = false
  IsoVisible = false
  LockPosition = true
  Perspective = false
  Rotation = 0
  RotationVector = (1,0,0)
  Scale = 0.25
  ScaleType = 2
  ScrubCount = 0
  SeamHidden = false
  SeamVisible = false
  SmoothHidden = false
  SmoothVisible = true
  Source = -> [Cut005_solid]
  Type = 0
  X = 0
  XDirection = (1,0,0)
  Y = 0
FEATURE [TechDraw::DrawProjGroupItem] ProjItem008  label="Left001"
  CoarseView = false
  Direction = (-1,-1e-16,0)
  Focus = 100
  HardHidden = false
  IsoCount = 0
  IsoHidden = false
  IsoVisible = false
  LockPosition = false
  Perspective = false
  Rotation = 0
  RotationVector = (1,0,0)
  Scale = 0.25
  ScaleType = 2
  ScrubCount = 0
  SeamHidden = false
  SeamVisible = false
  SmoothHidden = false
  SmoothVisible = true
  Source = -> [Cut005_solid]
  Type = 1
  X = 60.625
  XDirection = (1e-16,-1,0)
  Y = 0
FEATURE [TechDraw::DrawProjGroupItem] ProjItem009  label="Rear"
  CoarseView = false
  Direction = (0,1,0)
  Focus = 100
  HardHidden = false
  IsoCount = 0
  IsoHidden = false
  IsoVisible = false
  LockPosition = false
  Perspective = false
  Rotation = 0
  RotationVector = (1,0,0)
  Scale = 0.25
  ScaleType = 2
  ScrubCount = 0
  SeamHidden = false
  SeamVisible = false
  SmoothHidden = false
  SmoothVisible = true
  Source = -> [Cut005_solid]
  Type = 3
  X = 121.25
  XDirection = (-1,0,0)
  Y = 0
FEATURE [TechDraw::DrawProjGroup] ProjGroup003
  Anchor = -> ProjItem007
  AutoDistribute = true
  LockPosition = false
  ProjectionType = 0
  Rotation = 0
  Scale = 0.25
  ScaleType = 2
  Source = -> [Cut005_solid]
  Views = -> [ProjItem007,ProjItem008,ProjItem009]
  X = 81.5687
  Y = 134.106
  spacingX = 15
  spacingY = 15
FEATURE [TechDraw::DrawViewDimension] Dimension018
  AngleOverride = false
  Arbitrary = false
  ArbitraryTolerances = false
  EqualTolerance = true
  ExtensionAngle = 0
  FormatSpec = %.2w
  FormatSpecOverTolerance = %+.2w
  FormatSpecUnderTolerance = %+.2w
  Inverted = false
  LineAngle = 0
  LockPosition = false
  MeasureType = 1
  OverTolerance = 0
  References2D = -> [ProjItem008]
  Rotation = 0
  ScaleType = 0
  TheoreticalExact = false
  Type = 0
  UnderTolerance = 0
  X = -0.455383
  Y = -56.9653
FEATURE [TechDraw::DrawViewDimension] Dimension019
  AngleOverride = false
  Arbitrary = false
  ArbitraryTolerances = false
  EqualTolerance = true
  ExtensionAngle = 0
  FormatSpec = %.2w
  FormatSpecOverTolerance = %+.2w
  FormatSpecUnderTolerance = %+.2w
  Inverted = false
  LineAngle = 0
  LockPosition = false
  MeasureType = 1
  OverTolerance = 0
  References2D = -> [ProjItem007]
  Rotation = 0
  ScaleType = 0
  TheoreticalExact = false
  Type = 0
  UnderTolerance = 0
  X = 1.62527
  Y = -53.9348
FEATURE [TechDraw::DrawViewDimension] Dimension020
  AngleOverride = false
  Arbitrary = false
  ArbitraryTolerances = false
  EqualTolerance = true
  ExtensionAngle = 0
  FormatSpec = %.2w
  FormatSpecOverTolerance = %+.2w
  FormatSpecUnderTolerance = %+.2w
  Inverted = false
  LineAngle = 0
  LockPosition = false
  MeasureType = 1
  OverTolerance = 0
  References2D = -> [ProjItem007]
  Rotation = 0
  ScaleType = 0
  TheoreticalExact = false
  Type = 0
  UnderTolerance = 0
  X = 51.2951
  Y = 10.5618
FEATURE [TechDraw::DrawViewDimension] Dimension021
  AngleOverride = false
  Arbitrary = false
  ArbitraryTolerances = false
  EqualTolerance = true
  ExtensionAngle = 0
  FormatSpec = %.2w
  FormatSpecOverTolerance = %+.2w
  FormatSpecUnderTolerance = %+.2w
  Inverted = false
  LineAngle = 0
  LockPosition = false
  MeasureType = 1
  OverTolerance = 0
  References2D = -> [ProjItem007]
  Rotation = 0
  ScaleType = 0
  TheoreticalExact = false
  Type = 0
  UnderTolerance = 0
  X = -52.6258
  Y = -6.79175
FEATURE [TechDraw::DrawViewDimension] Dimension022
  AngleOverride = false
  Arbitrary = false
  ArbitraryTolerances = false
  EqualTolerance = true
  ExtensionAngle = 0
  FormatSpec = %.2w
  FormatSpecOverTolerance = %+.2w
  FormatSpecUnderTolerance = %+.2w
  Inverted = false
  LineAngle = 0
  LockPosition = false
  MeasureType = 1
  OverTolerance = 0
  References2D = -> [ProjItem007]
  Rotation = 0
  ScaleType = 0
  TheoreticalExact = false
  Type = 0
  UnderTolerance = 0
  X = 4.28564
  Y = 55.4175
FEATURE [TechDraw::DrawViewDimension] Dimension023
  AngleOverride = false
  Arbitrary = false
  ArbitraryTolerances = false
  EqualTolerance = true
  ExtensionAngle = 0
  FormatSpec = %.2w
  FormatSpecOverTolerance = %+.2w
  FormatSpecUnderTolerance = %+.2w
  Inverted = false
  LineAngle = 0
  LockPosition = false
  MeasureType = 1
  OverTolerance = 0
  References2D = -> [ProjItem007]
  Rotation = 0
  ScaleType = 0
  TheoreticalExact = false
  Type = 0
  UnderTolerance = 0
  X = 53.4271
  Y = 53.6905
FEATURE [TechDraw::DrawViewDimension] Dimension024
  AngleOverride = false
  Arbitrary = false
  ArbitraryTolerances = false
  EqualTolerance = true
  ExtensionAngle = 0
  FormatSpec = %.2w
  FormatSpecOverTolerance = %+.2w
  FormatSpecUnderTolerance = %+.2w
  Inverted = false
  LineAngle = 0
  LockPosition = false
  MeasureType = 1
  OverTolerance = 0
  References2D = -> [ProjItem007]
  Rotation = 0
  ScaleType = 0
  TheoreticalExact = false
  Type = 0
  UnderTolerance = 0
  X = 55.2543
  Y = 27.3383
FEATURE [TechDraw::DrawViewDimension] Dimension025
  AngleOverride = false
  Arbitrary = false
  ArbitraryTolerances = false
  EqualTolerance = true
  ExtensionAngle = 0
  FormatSpec = %.2w
  FormatSpecOverTolerance = %+.2w
  FormatSpecUnderTolerance = %+.2w
  Inverted = false
  LineAngle = 0
  LockPosition = false
  MeasureType = 1
  OverTolerance = 0
  References2D = -> [ProjItem007]
  Rotation = 0
  ScaleType = 0
  TheoreticalExact = false
  Type = 0
  UnderTolerance = 0
  X = -61.3154
  Y = 36.5853
FEATURE [TechDraw::DrawViewDimension] Dimension026
  AngleOverride = false
  Arbitrary = false
  ArbitraryTolerances = false
  EqualTolerance = true
  ExtensionAngle = 0
  FormatSpec = %.2w
  FormatSpecOverTolerance = %+.2w
  FormatSpecUnderTolerance = %+.2w
  Inverted = false
  LineAngle = 0
  LockPosition = false
  MeasureType = 1
  OverTolerance = 0
  References2D = -> [ProjItem007]
  Rotation = 0
  ScaleType = 0
  TheoreticalExact = false
  Type = 0
  UnderTolerance = 0
  X = 53.3157
  Y = -23.2461
FEATURE [TechDraw::DrawViewDimension] Dimension027
  AngleOverride = false
  Arbitrary = false
  ArbitraryTolerances = false
  EqualTolerance = true
  ExtensionAngle = 0
  FormatSpec = %.2w
  FormatSpecOverTolerance = %+.2w
  FormatSpecUnderTolerance = %+.2w
  Inverted = false
  LineAngle = 0
  LockPosition = false
  MeasureType = 1
  OverTolerance = 0
  References2D = -> [ProjItem007]
  Rotation = 0
  ScaleType = 0
  TheoreticalExact = false
  Type = 0
  UnderTolerance = 0
  X = 61.2148
  Y = -17.0615
FEATURE [TechDraw::DrawViewDimension] Dimension028
  AngleOverride = false
  Arbitrary = false
  ArbitraryTolerances = false
  EqualTolerance = true
  ExtensionAngle = 0
  FormatSpec = %.2w
  FormatSpecOverTolerance = %+.2w
  FormatSpecUnderTolerance = %+.2w
  Inverted = false
  LineAngle = 0
  LockPosition = false
  MeasureType = 1
  OverTolerance = 0
  References2D = -> [ProjItem007]
  Rotation = 0
  ScaleType = 0
  TheoreticalExact = false
  Type = 0
  UnderTolerance = 0
  X = -63.5403
  Y = -9.78076
FEATURE [TechDraw::DrawViewDimension] Dimension029
  AngleOverride = false
  Arbitrary = false
  ArbitraryTolerances = false
  EqualTolerance = true
  ExtensionAngle = 0
  FormatSpec = %.2w
  FormatSpecOverTolerance = %+.2w
  FormatSpecUnderTolerance = %+.2w
  Inverted = false
  LineAngle = 0
  LockPosition = false
  MeasureType = 1
  OverTolerance = 0
  References2D = -> [ProjItem007]
  Rotation = 0
  ScaleType = 0
  TheoreticalExact = false
  Type = 0
  UnderTolerance = 0
  X = -37.0905
  Y = -42.0346
FEATURE [TechDraw::DrawViewDimension] Dimension030
  AngleOverride = false
  Arbitrary = false
  ArbitraryTolerances = false
  EqualTolerance = true
  ExtensionAngle = 0
  FormatSpec = %.2w
  FormatSpecOverTolerance = %+.2w
  FormatSpecUnderTolerance = %+.2w
  Inverted = false
  LineAngle = 0
  LockPosition = false
  MeasureType = 1
  OverTolerance = 0
  References2D = -> [ProjItem007]
  Rotation = 0
  ScaleType = 0
  TheoreticalExact = false
  Type = 0
  UnderTolerance = 0
  X = -31.7918
  Y = -50.5054
FEATURE [TechDraw::DrawViewDimension] Dimension031
  AngleOverride = false
  Arbitrary = false
  ArbitraryTolerances = false
  EqualTolerance = true
  ExtensionAngle = 0
  FormatSpec = %.2w
  FormatSpecOverTolerance = %+.2w
  FormatSpecUnderTolerance = %+.2w
  Inverted = false
  LineAngle = 0
  LockPosition = false
  MeasureType = 1
  OverTolerance = 0
  References2D = -> [ProjItem007]
  Rotation = 0
  ScaleType = 0
  TheoreticalExact = false
  Type = 0
  UnderTolerance = 0
  X = 39.3494
  Y = -43.1246
FEATURE [TechDraw::DrawViewDimension] Dimension032
  AngleOverride = false
  Arbitrary = false
  ArbitraryTolerances = false
  EqualTolerance = true
  ExtensionAngle = 0
  FormatSpec = %.2w
  FormatSpecOverTolerance = %+.2w
  FormatSpecUnderTolerance = %+.2w
  Inverted = false
  LineAngle = 0
  LockPosition = false
  MeasureType = 1
  OverTolerance = 0
  References2D = -> [ProjItem007]
  Rotation = 0
  ScaleType = 0
  TheoreticalExact = false
  Type = 0
  UnderTolerance = 0
  X = 30.863
  Y = -51.1492
FEATURE [TechDraw::DrawViewDimension] Dimension033
  AngleOverride = false
  Arbitrary = false
  ArbitraryTolerances = false
  EqualTolerance = true
  ExtensionAngle = 0
  FormatSpec = %.2w
  FormatSpecOverTolerance = %+.2w
  FormatSpecUnderTolerance = %+.2w
  Inverted = false
  LineAngle = 0
  LockPosition = false
  MeasureType = 1
  OverTolerance = 0
  References2D = -> [ProjItem007]
  Rotation = 0
  ScaleType = 0
  TheoreticalExact = false
  Type = 0
  UnderTolerance = 0
  X = 16.0933
  Y = -33.0176
FEATURE [TechDraw::DrawViewDimension] Dimension034
  AngleOverride = false
  Arbitrary = false
  ArbitraryTolerances = false
  EqualTolerance = true
  ExtensionAngle = 0
  FormatSpec = %.2w
  FormatSpecOverTolerance = %+.2w
  FormatSpecUnderTolerance = %+.2w
  Inverted = false
  LineAngle = 0
  LockPosition = false
  MeasureType = 1
  OverTolerance = 0
  References2D = -> [ProjItem007]
  Rotation = 0
  ScaleType = 0
  TheoreticalExact = false
  Type = 0
  UnderTolerance = 0
  X = 31.9649
  Y = -20.6607
FEATURE [TechDraw::DrawViewDimension] Dimension035
  AngleOverride = false
  Arbitrary = false
  ArbitraryTolerances = false
  EqualTolerance = true
  ExtensionAngle = 0
  FormatSpec = %.2w
  FormatSpecOverTolerance = %+.2w
  FormatSpecUnderTolerance = %+.2w
  Inverted = false
  LineAngle = 0
  LockPosition = false
  MeasureType = 1
  OverTolerance = 0
  References2D = -> [ProjItem007]
  Rotation = 0
  ScaleType = 0
  TheoreticalExact = false
  Type = 0
  UnderTolerance = 0
  X = -65.9401
  Y = -44.1561
FEATURE [TechDraw::DrawViewDimension] Dimension036
  AngleOverride = false
  Arbitrary = false
  ArbitraryTolerances = false
  EqualTolerance = true
  ExtensionAngle = 0
  FormatSpec = ⌀%.2w
  FormatSpecOverTolerance = %+.2w
  FormatSpecUnderTolerance = %+.2w
  Inverted = false
  LineAngle = 0
  LockPosition = false
  MeasureType = 1
  OverTolerance = 0
  References2D = -> [ProjItem009]
  Rotation = 0
  ScaleType = 0
  TheoreticalExact = false
  Type = 5
  UnderTolerance = 0
  X = 14.1364
  Y = 53.9712
FEATURE [TechDraw::DrawViewDimension] Dimension037
  AngleOverride = false
  Arbitrary = false
  ArbitraryTolerances = false
  EqualTolerance = true
  ExtensionAngle = 0
  FormatSpec = ⌀%.2w
  FormatSpecOverTolerance = %+.2w
  FormatSpecUnderTolerance = %+.2w
  Inverted = false
  LineAngle = 0
  LockPosition = false
  MeasureType = 1
  OverTolerance = 0
  References2D = -> [ProjItem009]
  Rotation = 0
  ScaleType = 0
  TheoreticalExact = false
  Type = 5
  UnderTolerance = 0
  X = 4.18046
  Y = 56.3026
FEATURE [TechDraw::DrawViewDimension] Dimension038
  AngleOverride = false
  Arbitrary = false
  ArbitraryTolerances = false
  EqualTolerance = true
  ExtensionAngle = 0
  FormatSpec = ⌀%.2w
  FormatSpecOverTolerance = %+.2w
  FormatSpecUnderTolerance = %+.2w
  Inverted = false
  LineAngle = 0
  LockPosition = false
  MeasureType = 1
  OverTolerance = 0
  References2D = -> [ProjItem009]
  Rotation = 0
  ScaleType = 0
  TheoreticalExact = false
  Type = 5
  UnderTolerance = 0
  X = -5.85152
  Y = 56.7105
FEATURE [TechDraw::DrawViewDimension] Dimension039
  AngleOverride = false
  Arbitrary = false
  ArbitraryTolerances = false
  EqualTolerance = true
  ExtensionAngle = 0
  FormatSpec = ⌀%.2w
  FormatSpecOverTolerance = %+.2w
  FormatSpecUnderTolerance = %+.2w
  Inverted = false
  LineAngle = 0
  LockPosition = false
  MeasureType = 1
  OverTolerance = 0
  References2D = -> [ProjItem009]
  Rotation = 0
  ScaleType = 0
  TheoreticalExact = false
  Type = 5
  UnderTolerance = 0
  X = -15.1276
  Y = 52.7487
FEATURE [TechDraw::DrawViewDimension] Dimension040
  AngleOverride = false
  Arbitrary = false
  ArbitraryTolerances = false
  EqualTolerance = true
  ExtensionAngle = 0
  FormatSpec = %.2w
  FormatSpecOverTolerance = %+.2w
  FormatSpecUnderTolerance = %+.2w
  Inverted = false
  LineAngle = 0
  LockPosition = false
  MeasureType = 1
  OverTolerance = 0
  References2D = -> [ProjItem009]
  Rotation = 0
  ScaleType = 0
  TheoreticalExact = false
  Type = 0
  UnderTolerance = 0
  X = -49.4687
  Y = 39.7862
FEATURE [TechDraw::DrawViewDimension] Dimension042
  AngleOverride = false
  Arbitrary = false
  ArbitraryTolerances = false
  EqualTolerance = true
  ExtensionAngle = 0
  FormatSpec = %.2w
  FormatSpecOverTolerance = %+.2w
  FormatSpecUnderTolerance = %+.2w
  Inverted = false
  LineAngle = 0
  LockPosition = false
  MeasureType = 1
  OverTolerance = 0
  References2D = -> [ProjItem009]
  Rotation = 0
  ScaleType = 0
  TheoreticalExact = false
  Type = 0
  UnderTolerance = 0
  X = -38.3525
  Y = 52.7118
FEATURE [TechDraw::DrawViewDimension] Dimension043
  AngleOverride = false
  Arbitrary = false
  ArbitraryTolerances = false
  EqualTolerance = true
  ExtensionAngle = 0
  FormatSpec = %.2w
  FormatSpecOverTolerance = %+.2w
  FormatSpecUnderTolerance = %+.2w
  Inverted = false
  LineAngle = 0
  LockPosition = false
  MeasureType = 1
  OverTolerance = 0
  References2D = -> [ProjItem009]
  Rotation = 0
  ScaleType = 0
  TheoreticalExact = false
  Type = 0
  UnderTolerance = 0
  X = 47.3667
  Y = 42.5145
FEATURE [TechDraw::DrawViewDimension] Dimension044
  AngleOverride = false
  Arbitrary = false
  ArbitraryTolerances = false
  EqualTolerance = true
  ExtensionAngle = 0
  FormatSpec = %.2w
  FormatSpecOverTolerance = %+.2w
  FormatSpecUnderTolerance = %+.2w
  Inverted = false
  LineAngle = 0
  LockPosition = false
  MeasureType = 1
  OverTolerance = 0
  References2D = -> [ProjItem009]
  Rotation = 0
  ScaleType = 0
  TheoreticalExact = false
  Type = 1
  UnderTolerance = 0
  X = 37.5557
  Y = 56.6858
FEATURE [TechDraw::DrawViewDimension] Dimension045
  AngleOverride = false
  Arbitrary = false
  ArbitraryTolerances = false
  EqualTolerance = true
  ExtensionAngle = 0
  FormatSpec = %.2w
  FormatSpecOverTolerance = %+.2w
  FormatSpecUnderTolerance = %+.2w
  Inverted = false
  LineAngle = 0
  LockPosition = false
  MeasureType = 1
  OverTolerance = 0
  References2D = -> [ProjItem009]
  Rotation = 0
  ScaleType = 0
  TheoreticalExact = false
  Type = 0
  UnderTolerance = 0
  X = -46.6179
  Y = -34.9673
FEATURE [TechDraw::DrawViewDimension] Dimension046
  AngleOverride = false
  Arbitrary = false
  ArbitraryTolerances = false
  EqualTolerance = true
  ExtensionAngle = 0
  FormatSpec = %.2w
  FormatSpecOverTolerance = %+.2w
  FormatSpecUnderTolerance = %+.2w
  Inverted = false
  LineAngle = 0
  LockPosition = false
  MeasureType = 1
  OverTolerance = 0
  References2D = -> [ProjItem009]
  Rotation = 0
  ScaleType = 0
  TheoreticalExact = false
  Type = 0
  UnderTolerance = 0
  X = 38.0175
  Y = -43.4232
FEATURE [TechDraw::DrawPage] Page002  label="FrontDoorDrawing01"
  KeepUpdated = true
  NextBalloonIndex = 1
  ProjectionType = 0
  Template = -> Template002
  Views = -> [ProjGroup003,Dimension018,Dimension019,Dimension020,Dimension021,Dimension022,Dimension023,Dimension024,Dimension025,Dimension026,Dimension027,Dimension028,Dimension029,Dimension030,Dimension031,Dimension032,Dimension033,Dimension034,Dimension035,Dimension036,Dimension037,Dimension038,Dimension039,Dimension040,Dimension042,Dimension043,Dimension044,Dimension045,Dimension046]
FEATURE [TechDraw::DrawSVGTemplate] Template003
  EditableTexts = Designed_by_Name=Thomas Spielauer; FC-Date=2023-09-05; FC-SC=mm; FC-SH=2/5; FC-Title=XL30 compatible flange door; Subtitle=Main door flanges
  Height = 210
  Orientation = 1
  Template = <path>
  Width = 297
FEATURE [TechDraw::DrawViewPart] View
  CoarseView = false
  Direction = (0,-1,0)
  Focus = 100
  HardHidden = false
  IsoCount = 0
  IsoHidden = false
  IsoVisible = false
  LockPosition = false
  Perspective = false
  Rotation = 0
  Scale = 0.3
  ScaleType = 2
  ScrubCount = 0
  SeamHidden = false
  SeamVisible = false
  SmoothHidden = false
  SmoothVisible = true
  Source = -> [Cut005_solid]
  X = 79.773
  XDirection = (1,0,0)
  Y = 133.736
FEATURE [TechDraw::DrawViewSection] SectionView002  label="Section  - 002"
  BaseView = -> View
  CoarseView = false
  CutSurfaceDisplay = 2
  Direction = (-1,0,-1e-16)
  FileGeomPattern = <path>
  FileHatchPattern = <path>
  Focus = 100
  FuseBeforeCut = false
  HardHidden = false
  HatchOffset = (0,0,0)
  HatchRotation = 0
  HatchScale = 1
  IsoCount = 0
  IsoHidden = false
  IsoVisible = false
  LockPosition = false
  NameGeomPattern = Diamant
  Perspective = false
  Rotation = -90
  Scale = 0.3
  ScaleType = 2
  ScrubCount = 0
  SeamHidden = false
  SeamVisible = false
  SectionDirection = 4
  SectionNormal = (-1,0,-1e-16)
  SectionOrigin = (165,17.5,165)
  SmoothHidden = false
  SmoothVisible = true
  Source = -> [Cut005_solid]
  TrimAfterCut = false
  X = 176.867
  XDirection = (1e-16,0,-1)
  Y = 135.976
FEATURE [TechDraw::DrawViewDimension] Dimension047
  AngleOverride = false
  Arbitrary = false
  ArbitraryTolerances = false
  EqualTolerance = true
  ExtensionAngle = 0
  FormatSpec = %.2w
  FormatSpecOverTolerance = %+.2w
  FormatSpecUnderTolerance = %+.2w
  Inverted = false
  LineAngle = 0
  LockPosition = false
  MeasureType = 1
  OverTolerance = 0
  References2D = -> [View]
  Rotation = 0
  Scale = 0.2
  ScaleType = 0
  TheoreticalExact = false
  Type = 6
  UnderTolerance = 0
  X = -24.618
  Y = 24.6806
FEATURE [TechDraw::DrawViewDimension] Dimension048
  AngleOverride = false
  Arbitrary = false
  ArbitraryTolerances = false
  EqualTolerance = true
  ExtensionAngle = 0
  FormatSpec = ⌀%.2w
  FormatSpecOverTolerance = %+.2w
  FormatSpecUnderTolerance = %+.2w
  Inverted = false
  LineAngle = 0
  LockPosition = false
  MeasureType = 1
  OverTolerance = 0
  References2D = -> [View]
  Rotation = 0
  Scale = 0.2
  ScaleType = 0
  TheoreticalExact = false
  Type = 5
  UnderTolerance = 0
  X = -50.8548
  Y = 19.0195
FEATURE [TechDraw::DrawViewDimension] Dimension049
  AngleOverride = false
  Arbitrary = false
  ArbitraryTolerances = false
  EqualTolerance = true
  ExtensionAngle = 0
  FormatSpec = ⌀%.2w (32x M6)
  FormatSpecOverTolerance = %+.2w
  FormatSpecUnderTolerance = %+.2w
  Inverted = false
  LineAngle = 0
  LockPosition = false
  MeasureType = 1
  OverTolerance = 0
  References2D = -> [View]
  Rotation = 0
  Scale = 0.2
  ScaleType = 0
  TheoreticalExact = false
  Type = 5
  UnderTolerance = 0
  X = -55.0956
  Y = -34.3132
FEATURE [TechDraw::DrawViewDimension] Dimension050
  AngleOverride = false
  Arbitrary = false
  ArbitraryTolerances = false
  EqualTolerance = true
  ExtensionAngle = 0
  FormatSpec = %.2w
  FormatSpecOverTolerance = %+.2w
  FormatSpecUnderTolerance = %+.2w
  Inverted = false
  LineAngle = 0
  LockPosition = false
  MeasureType = 1
  OverTolerance = 0
  References2D = -> [SectionView002]
  Rotation = 0
  Scale = 0.2
  ScaleType = 0
  TheoreticalExact = false
  Type = 0
  UnderTolerance = 0
  X = 20.4023
  Y = 22.9741
FEATURE [TechDraw::DrawViewDimension] Dimension051
  AngleOverride = false
  Arbitrary = false
  ArbitraryTolerances = false
  EqualTolerance = true
  ExtensionAngle = 0
  FormatSpec = %.2w (Seal groove)
  FormatSpecOverTolerance = %+.2w
  FormatSpecUnderTolerance = %+.2w
  Inverted = false
  LineAngle = 0
  LockPosition = false
  MeasureType = 1
  OverTolerance = 0
  References2D = -> [SectionView002]
  Rotation = 0
  Scale = 0.2
  ScaleType = 0
  TheoreticalExact = false
  Type = 0
  UnderTolerance = 0
  X = 48.9949
  Y = 7.05707
FEATURE [TechDraw::DrawViewDimension] Dimension052
  AngleOverride = false
  Arbitrary = false
  ArbitraryTolerances = false
  EqualTolerance = true
  ExtensionAngle = 0
  FormatSpec = %.2w
  FormatSpecOverTolerance = %+.2w
  FormatSpecUnderTolerance = %+.2w
  Inverted = false
  LineAngle = 0
  LockPosition = false
  MeasureType = 1
  OverTolerance = 0
  References2D = -> [SectionView002]
  Rotation = 0
  Scale = 0.2
  ScaleType = 0
  TheoreticalExact = false
  Type = 2
  UnderTolerance = 0
  X = 30.2572
  Y = 22.771
FEATURE [TechDraw::DrawViewDimension] Dimension053
  AngleOverride = false
  Arbitrary = false
  ArbitraryTolerances = false
  EqualTolerance = true
  ExtensionAngle = 0
  FormatSpec = %.2w
  FormatSpecOverTolerance = %+.2w
  FormatSpecUnderTolerance = %+.2w
  Inverted = false
  LineAngle = 0
  LockPosition = false
  MeasureType = 1
  OverTolerance = 0
  References2D = -> [SectionView002]
  Rotation = 0
  Scale = 0.2
  ScaleType = 0
  TheoreticalExact = false
  Type = 0
  UnderTolerance = 0
  X = 3.54931
  Y = 59.7192
FEATURE [TechDraw::DrawViewDimension] Dimension054
  AngleOverride = false
  Arbitrary = false
  ArbitraryTolerances = false
  EqualTolerance = true
  ExtensionAngle = 0
  FormatSpec = %.2w (M8)
  FormatSpecOverTolerance = %+.2w
  FormatSpecUnderTolerance = %+.2w
  Inverted = false
  LineAngle = 0
  LockPosition = false
  MeasureType = 1
  OverTolerance = 0
  References2D = -> [SectionView002]
  Rotation = 0
  Scale = 0.2
  ScaleType = 0
  TheoreticalExact = false
  Type = 0
  UnderTolerance = 0
  X = 27.5113
  Y = 51.2625
FEATURE [TechDraw::DrawViewAnnotation] Annotation002
  Font = osifont
  LineSpace = 100
  LockPosition = false
  MaxWidth = -1
  Rotation = 0
  Scale = 0.2
  ScaleType = 0
  Text = Note: The 8mm seal grove is not CF compliant | One can use Viton Gaskets betwen a CF flange | and those grooves for sealing like elsewhere on | the SEM.
  TextSize = 3
  TextStyle = 0
  X = 242.711
  Y = 89.7467
FEATURE [TechDraw::DrawViewDimension] Dimension055
  AngleOverride = false
  Arbitrary = false
  ArbitraryTolerances = false
  EqualTolerance = true
  ExtensionAngle = 0
  FormatSpec = %.2w
  FormatSpecOverTolerance = %+.2w
  FormatSpecUnderTolerance = %+.2w
  Inverted = false
  LineAngle = 0
  LockPosition = false
  MeasureType = 1
  OverTolerance = 0
  References2D = -> [SectionView002]
  Rotation = 0
  Scale = 0.2
  ScaleType = 0
  TheoreticalExact = false
  Type = 0
  UnderTolerance = 0
  X = -3.49137
  Y = 63.5264
FEATURE [TechDraw::DrawViewSection] SectionView003  label="Section  - 003"
  BaseView = -> View
  CoarseView = false
  CutSurfaceDisplay = 2
  Direction = (1e-16,0,1)
  FileGeomPattern = <path>
  FileHatchPattern = <path>
  Focus = 100
  FuseBeforeCut = false
  HardHidden = false
  HatchOffset = (0,0,0)
  HatchRotation = 0
  HatchScale = 1
  IsoCount = 0
  IsoHidden = false
  IsoVisible = false
  LockPosition = false
  NameGeomPattern = Diamant
  Perspective = false
  Rotation = 0
  Scale = 0.3
  ScaleType = 2
  ScrubCount = 0
  SeamHidden = false
  SeamVisible = false
  SectionDirection = 4
  SectionNormal = (1e-16,0,1)
  SectionOrigin = (165,16.5,35)
  SmoothHidden = false
  SmoothVisible = true
  Source = -> [Cut005_solid]
  TrimAfterCut = false
  X = 84.6457
  XDirection = (1,0,-1e-16)
  Y = 47.8352
FEATURE [TechDraw::DrawViewDimension] Dimension056
  AngleOverride = false
  Arbitrary = false
  ArbitraryTolerances = false
  EqualTolerance = true
  ExtensionAngle = 0
  FormatSpec = %.2w
  FormatSpecOverTolerance = %+.2w
  FormatSpecUnderTolerance = %+.2w
  Inverted = false
  LineAngle = 0
  LockPosition = false
  MeasureType = 1
  OverTolerance = 0
  References2D = -> [SectionView003]
  Rotation = 0
  Scale = 0.2
  ScaleType = 0
  TheoreticalExact = false
  Type = 0
  UnderTolerance = 0
  X = -61.9395
  Y = -6.96394
FEATURE [TechDraw::DrawViewDimension] Dimension057
  AngleOverride = false
  Arbitrary = false
  ArbitraryTolerances = false
  EqualTolerance = true
  ExtensionAngle = 0
  FormatSpec = %.2w
  FormatSpecOverTolerance = %+.2w
  FormatSpecUnderTolerance = %+.2w
  Inverted = false
  LineAngle = 0
  LockPosition = false
  MeasureType = 1
  OverTolerance = 0
  References2D = -> [SectionView003]
  Rotation = 0
  Scale = 0.2
  ScaleType = 0
  TheoreticalExact = false
  Type = 0
  UnderTolerance = 0
  X = -58.567
  Y = 13.7001
FEATURE [TechDraw::DrawViewDimension] Dimension058
  AngleOverride = false
  Arbitrary = false
  ArbitraryTolerances = false
  EqualTolerance = true
  ExtensionAngle = 0
  FormatSpec = %.2w
  FormatSpecOverTolerance = %+.2w
  FormatSpecUnderTolerance = %+.2w
  Inverted = false
  LineAngle = 0
  LockPosition = false
  MeasureType = 1
  OverTolerance = 0
  References2D = -> [SectionView003]
  Rotation = 0
  Scale = 0.2
  ScaleType = 0
  TheoreticalExact = false
  Type = 0
  UnderTolerance = 0
  X = 56.4178
  Y = -7.68117
FEATURE [TechDraw::DrawViewDimension] Dimension059
  AngleOverride = false
  Arbitrary = false
  ArbitraryTolerances = false
  EqualTolerance = true
  ExtensionAngle = 0
  FormatSpec = %.2w
  FormatSpecOverTolerance = %+.2w
  FormatSpecUnderTolerance = %+.2w
  Inverted = false
  LineAngle = 0
  LockPosition = false
  MeasureType = 1
  OverTolerance = 0
  References2D = -> [SectionView003]
  Rotation = 0
  Scale = 0.2
  ScaleType = 0
  TheoreticalExact = false
  Type = 0
  UnderTolerance = 0
  X = 59.6522
  Y = 12.8678
FEATURE [TechDraw::DrawPage] Page003  label="FrontDoorDrawing02"
  KeepUpdated = true
  NextBalloonIndex = 1
  ProjectionType = 0
  Scale = 0.2
  Template = -> Template003
  Views = -> [View,SectionView002,Dimension047,Dimension048,Dimension049,Dimension050,Dimension051,Dimension052,Dimension053,Dimension054,Annotation002,Dimension055,SectionView003,Dimension056,Dimension057,Dimension058,Dimension059]
FEATURE [TechDraw::DrawSVGTemplate] Template004
  EditableTexts = Designed_by_Name=Thomas Spielauer; Drawing_number=1; FC-Date=2023-09-05; FC-SC=mm; FC-SH=3/5; FC-Title=XL30 compatible flange door; Subtitle=Seal backside
  Height = 210
  Orientation = 1
  Template = <path>
  Width = 297
FEATURE [TechDraw::DrawProjGroupItem] ProjItem010  label="Front003"
  CoarseView = false
  Direction = (0,1,0)
  Focus = 100
  HardHidden = false
  IsoCount = 0
  IsoHidden = false
  IsoVisible = false
  LockPosition = true
  Perspective = false
  Rotation = 0
  RotationVector = (-1,0,0)
  Scale = 0.25
  ScaleType = 2
  ScrubCount = 0
  SeamHidden = false
  SeamVisible = false
  SmoothHidden = false
  SmoothVisible = true
  Source = -> [Cut005_solid]
  Type = 0
  X = 0
  XDirection = (-1,0,0)
  Y = 0
FEATURE [TechDraw::DrawProjGroup] ProjGroup004
  Anchor = -> ProjItem010
  AutoDistribute = true
  LockPosition = false
  ProjectionType = 0
  Rotation = 0
  Scale = 0.25
  ScaleType = 2
  Source = -> [Cut005_solid]
  Views = -> [ProjItem010]
  X = 78.0561
  Y = 136.828
  spacingX = 15
  spacingY = 15
FEATURE [TechDraw::DrawViewDimension] Dimension060
  AngleOverride = false
  Arbitrary = false
  ArbitraryTolerances = false
  EqualTolerance = true
  ExtensionAngle = 0
  FormatSpec = ⌀%.2w
  FormatSpecOverTolerance = %+.2w
  FormatSpecUnderTolerance = %+.2w
  Inverted = false
  LineAngle = 0
  LockPosition = false
  MeasureType = 1
  OverTolerance = 0
  References2D = -> [ProjItem010]
  Rotation = 0
  ScaleType = 0
  TheoreticalExact = false
  Type = 5
  UnderTolerance = 0
  X = 60.7645
  Y = 19.3017
FEATURE [TechDraw::DrawViewDimension] Dimension061
  AngleOverride = false
  Arbitrary = false
  ArbitraryTolerances = false
  EqualTolerance = true
  ExtensionAngle = 0
  FormatSpec = ⌀%.2w
  FormatSpecOverTolerance = %+.2w
  FormatSpecUnderTolerance = %+.2w
  Inverted = false
  LineAngle = 0
  LockPosition = false
  MeasureType = 1
  OverTolerance = 0
  References2D = -> [ProjItem010]
  Rotation = 0
  ScaleType = 0
  TheoreticalExact = false
  Type = 5
  UnderTolerance = 0
  X = 61.4088
  Y = 11.8508
FEATURE [TechDraw::DrawViewDimension] Dimension062
  AngleOverride = false
  Arbitrary = false
  ArbitraryTolerances = false
  EqualTolerance = true
  ExtensionAngle = 0
  FormatSpec = ⌀%.2w
  FormatSpecOverTolerance = %+.2w
  FormatSpecUnderTolerance = %+.2w
  Inverted = false
  LineAngle = 0
  LockPosition = false
  MeasureType = 1
  OverTolerance = 0
  References2D = -> [ProjItem010]
  Rotation = 0
  ScaleType = 0
  TheoreticalExact = false
  Type = 5
  UnderTolerance = 0
  X = 60.7355
  Y = 3.09738
FEATURE [TechDraw::DrawViewSection] SectionView004  label="Section  - 004"
  BaseView = -> ProjItem010
  CoarseView = false
  CutSurfaceDisplay = 2
  Direction = (1,0,-1e-16)
  FileGeomPattern = <path>
  FileHatchPattern = <path>
  Focus = 100
  FuseBeforeCut = false
  HardHidden = false
  HatchOffset = (0,0,0)
  HatchRotation = 0
  HatchScale = 1
  IsoCount = 0
  IsoHidden = false
  IsoVisible = false
  LockPosition = false
  NameGeomPattern = Diamant
  Perspective = false
  Rotation = -90
  Scale = 0.4
  ScaleType = 2
  ScrubCount = 0
  SeamHidden = false
  SeamVisible = false
  SectionDirection = 4
  SectionNormal = (1,0,-1e-16)
  SectionOrigin = (165,17.5,165)
  SmoothHidden = false
  SmoothVisible = true
  Source = -> [Cut005_solid]
  TrimAfterCut = false
  X = 197.856
  XDirection = (-1e-16,0,-1)
  Y = 131.124
FEATURE [TechDraw::DrawViewDimension] Dimension063
  AngleOverride = false
  Arbitrary = false
  ArbitraryTolerances = false
  EqualTolerance = true
  ExtensionAngle = 0
  FormatSpec = %.2w
  FormatSpecOverTolerance = %+.2w
  FormatSpecUnderTolerance = %+.2w
  Inverted = false
  LineAngle = 0
  LockPosition = false
  MeasureType = 1
  OverTolerance = 0
  References2D = -> [SectionView004]
  Rotation = 0
  ScaleType = 0
  TheoreticalExact = false
  Type = 0
  UnderTolerance = 0
  X = 26.0342
  Y = -56.5996
FEATURE [TechDraw::DrawViewDimension] Dimension064
  AngleOverride = false
  Arbitrary = false
  ArbitraryTolerances = false
  EqualTolerance = true
  ExtensionAngle = 0
  FormatSpec = %.2w
  FormatSpecOverTolerance = %+.2w
  FormatSpecUnderTolerance = %+.2w
  Inverted = false
  LineAngle = 0
  LockPosition = false
  MeasureType = 1
  OverTolerance = 0
  References2D = -> [SectionView004]
  Rotation = 0
  ScaleType = 0
  TheoreticalExact = false
  Type = 1
  UnderTolerance = 0
  X = -12.9367
  Y = -62.6793
FEATURE [TechDraw::DrawViewDimension] Dimension065
  AngleOverride = false
  Arbitrary = false
  ArbitraryTolerances = false
  EqualTolerance = true
  ExtensionAngle = 0
  FormatSpec = %.2w
  FormatSpecOverTolerance = %+.2w
  FormatSpecUnderTolerance = %+.2w
  Inverted = false
  LineAngle = 0
  LockPosition = false
  MeasureType = 1
  OverTolerance = 0
  References2D = -> [SectionView004]
  Rotation = 0
  ScaleType = 0
  TheoreticalExact = false
  Type = 0
  UnderTolerance = 0
  X = 34.4112
  Y = -60.1581
FEATURE [TechDraw::DrawViewDimension] Dimension066
  AngleOverride = false
  Arbitrary = false
  ArbitraryTolerances = false
  EqualTolerance = true
  ExtensionAngle = 0
  FormatSpec = %.2w
  FormatSpecOverTolerance = %+.2w
  FormatSpecUnderTolerance = %+.2w
  Inverted = false
  LineAngle = 0
  LockPosition = false
  MeasureType = 1
  OverTolerance = 0
  References2D = -> [SectionView004]
  Rotation = 0
  ScaleType = 0
  TheoreticalExact = false
  Type = 0
  UnderTolerance = 0
  X = 18.6451
  Y = -51.9238
FEATURE [TechDraw::DrawViewDimension] Dimension067
  AngleOverride = false
  Arbitrary = false
  ArbitraryTolerances = false
  EqualTolerance = true
  ExtensionAngle = 0
  FormatSpec = %.2w
  FormatSpecOverTolerance = %+.2w
  FormatSpecUnderTolerance = %+.2w
  Inverted = false
  LineAngle = 0
  LockPosition = false
  MeasureType = 1
  OverTolerance = 0
  References2D = -> [SectionView004]
  Rotation = 0
  ScaleType = 0
  TheoreticalExact = false
  Type = 0
  UnderTolerance = 0
  X = 17.7869
  Y = -41.6353
FEATURE [TechDraw::DrawPage] Page004  label="FrontDoorDrawing03"
  KeepUpdated = true
  NextBalloonIndex = 1
  ProjectionType = 0
  Template = -> Template004
  Views = -> [ProjGroup004,Dimension060,Dimension061,Dimension062,SectionView004,Dimension063,Dimension064,Dimension065,Dimension066,Dimension067]
FEATURE [TechDraw::DrawSVGTemplate] Template005
  EditableTexts = Designed_by_Name=Thomas Spielauer; FC-Date=2023-09-05; FC-SC=mm; FC-SH=4/5; FC-Title=XL30 compatible flange door; Subtitle=Handle attachment
  Height = 210
  Orientation = 1
  Template = <path>
  Width = 297
FEATURE [TechDraw::DrawProjGroupItem] ProjItem011  label="Front004"
  CoarseView = false
  Direction = (-1e-06,-1,0)
  Focus = 100
  HardHidden = false
  IsoCount = 0
  IsoHidden = false
  IsoVisible = false
  LockPosition = true
  Perspective = false
  Rotation = 0
  RotationVector = (1,-1e-06,0)
  Scale = 0.2
  ScaleType = 2
  ScrubCount = 0
  SeamHidden = false
  SeamVisible = false
  SmoothHidden = false
  SmoothVisible = true
  Source = -> [Cut005_solid]
  Type = 0
  X = 0
  XDirection = (1,-1e-06,0)
  Y = 0
FEATURE [TechDraw::DrawProjGroup] ProjGroup005
  Anchor = -> ProjItem011
  AutoDistribute = true
  LockPosition = false
  ProjectionType = 0
  Rotation = 0
  Scale = 0.2
  ScaleType = 2
  Source = -> [Cut005_solid]
  Views = -> [ProjItem011]
  X = 68.0337
  Y = 154.387
  spacingX = 15
  spacingY = 15
FEATURE [TechDraw::DrawViewSection] SectionView005  label="Section  - 005"
  BaseView = -> ProjItem011
  CoarseView = false
  CutSurfaceDisplay = 2
  Direction = (0,0,1)
  FileGeomPattern = <path>
  FileHatchPattern = <path>
  Focus = 100
  FuseBeforeCut = false
  HardHidden = false
  HatchOffset = (0,0,0)
  HatchRotation = 0
  HatchScale = 1
  IsoCount = 0
  IsoHidden = false
  IsoVisible = false
  LockPosition = false
  NameGeomPattern = Diamant
  Perspective = false
  Rotation = 0
  Scale = 0.6
  ScaleType = 2
  ScrubCount = 0
  SeamHidden = false
  SeamVisible = false
  SectionDirection = 4
  SectionNormal = (0,0,1)
  SectionOrigin = (165,17.5,40)
  SmoothHidden = false
  SmoothVisible = true
  Source = -> [Cut005_solid]
  TrimAfterCut = false
  X = 126.368
  XDirection = (1,-1e-06,0)
  Y = 88.6062
FEATURE [TechDraw::DrawViewDimension] Dimension068
  AngleOverride = false
  Arbitrary = false
  ArbitraryTolerances = false
  EqualTolerance = true
  ExtensionAngle = 0
  FormatSpec = %.2w
  FormatSpecOverTolerance = %+.2w
  FormatSpecUnderTolerance = %+.2w
  Inverted = false
  LineAngle = 0
  LockPosition = false
  MeasureType = 1
  OverTolerance = 0
  References2D = -> [SectionView005]
  Rotation = 0
  ScaleType = 0
  TheoreticalExact = false
  Type = 0
  UnderTolerance = 0
  X = -105.117
  Y = -10.2011
FEATURE [TechDraw::DrawViewDimension] Dimension069
  AngleOverride = false
  Arbitrary = false
  ArbitraryTolerances = false
  EqualTolerance = true
  ExtensionAngle = 0
  FormatSpec = %.2w
  FormatSpecOverTolerance = %+.2w
  FormatSpecUnderTolerance = %+.2w
  Inverted = false
  LineAngle = 0
  LockPosition = false
  MeasureType = 1
  OverTolerance = 0
  References2D = -> [SectionView005]
  Rotation = 0
  ScaleType = 0
  TheoreticalExact = false
  Type = 0
  UnderTolerance = 0
  X = -108.758
  Y = 11.4512
FEATURE [TechDraw::DrawPage] Page005  label="FrontDoorDrawing04"
  KeepUpdated = true
  NextBalloonIndex = 1
  ProjectionType = 0
  Template = -> Template005
  Views = -> [ProjGroup005,SectionView005,Dimension068,Dimension069]
FEATURE [TechDraw::DrawSVGTemplate] Template006
  EditableTexts = Designed_by_Name=Thomas Spielauer; FC-Date=2023-09-05; FC-SH=5/5; FC-Title=XL30 compatible flange door; Subtitle=Overview
  Height = 210
  Orientation = 1
  Template = <path>
  Width = 297
FEATURE [TechDraw::DrawProjGroupItem] ProjItem012  label="Front005"
  CoarseView = false
  Direction = (0.57735,-0.57735,0.57735)
  Focus = 100
  HardHidden = false
  IsoCount = 0
  IsoHidden = false
  IsoVisible = false
  LockPosition = true
  Perspective = false
  Rotation = 0
  RotationVector = (0.707107,0.707107,-5.7735e-07)
  Scale = 0.25
  ScaleType = 2
  ScrubCount = 0
  SeamHidden = false
  SeamVisible = false
  SmoothHidden = false
  SmoothVisible = true
  Source = -> [Cut005_solid]
  Type = 0
  X = 0
  XDirection = (0.707107,0.707107,-5.7735e-07)
  Y = 0
FEATURE [TechDraw::DrawProjGroupItem] ProjItem013  label="Rear001"
  CoarseView = false
  Direction = (-0.57735,0.57735,-0.57735)
  Focus = 100
  HardHidden = false
  IsoCount = 0
  IsoHidden = false
  IsoVisible = false
  LockPosition = false
  Perspective = false
  Rotation = 0
  RotationVector = (1,0,0)
  ScaleType = 2
  ScrubCount = 0
  SeamHidden = false
  SeamVisible = false
  SmoothHidden = false
  SmoothVisible = true
  Source = -> [Cut005_solid]
  Type = 3
  X = 107.318
  XDirection = (-0.707107,-0.707106,5.7735e-07)
  Y = 0
FEATURE [TechDraw::DrawProjGroup] ProjGroup006
  Anchor = -> ProjItem012
  AutoDistribute = true
  LockPosition = false
  ProjectionType = 0
  Rotation = 0
  Scale = 0.25
  ScaleType = 2
  Source = -> [Cut005_solid]
  Views = -> [ProjItem012,ProjItem013]
  X = 93.3324
  Y = 132.434
  spacingX = 15
  spacingY = 15
FEATURE [TechDraw::DrawPage] Page006  label="FrontDoorDrawing05"
  KeepUpdated = true
  NextBalloonIndex = 1
  ProjectionType = 0
  Template = -> Template006
  Views = -> [ProjGroup006]
note: 19 file-system paths scrubbed to <path> (originals preserved in the JSON sidecar)
